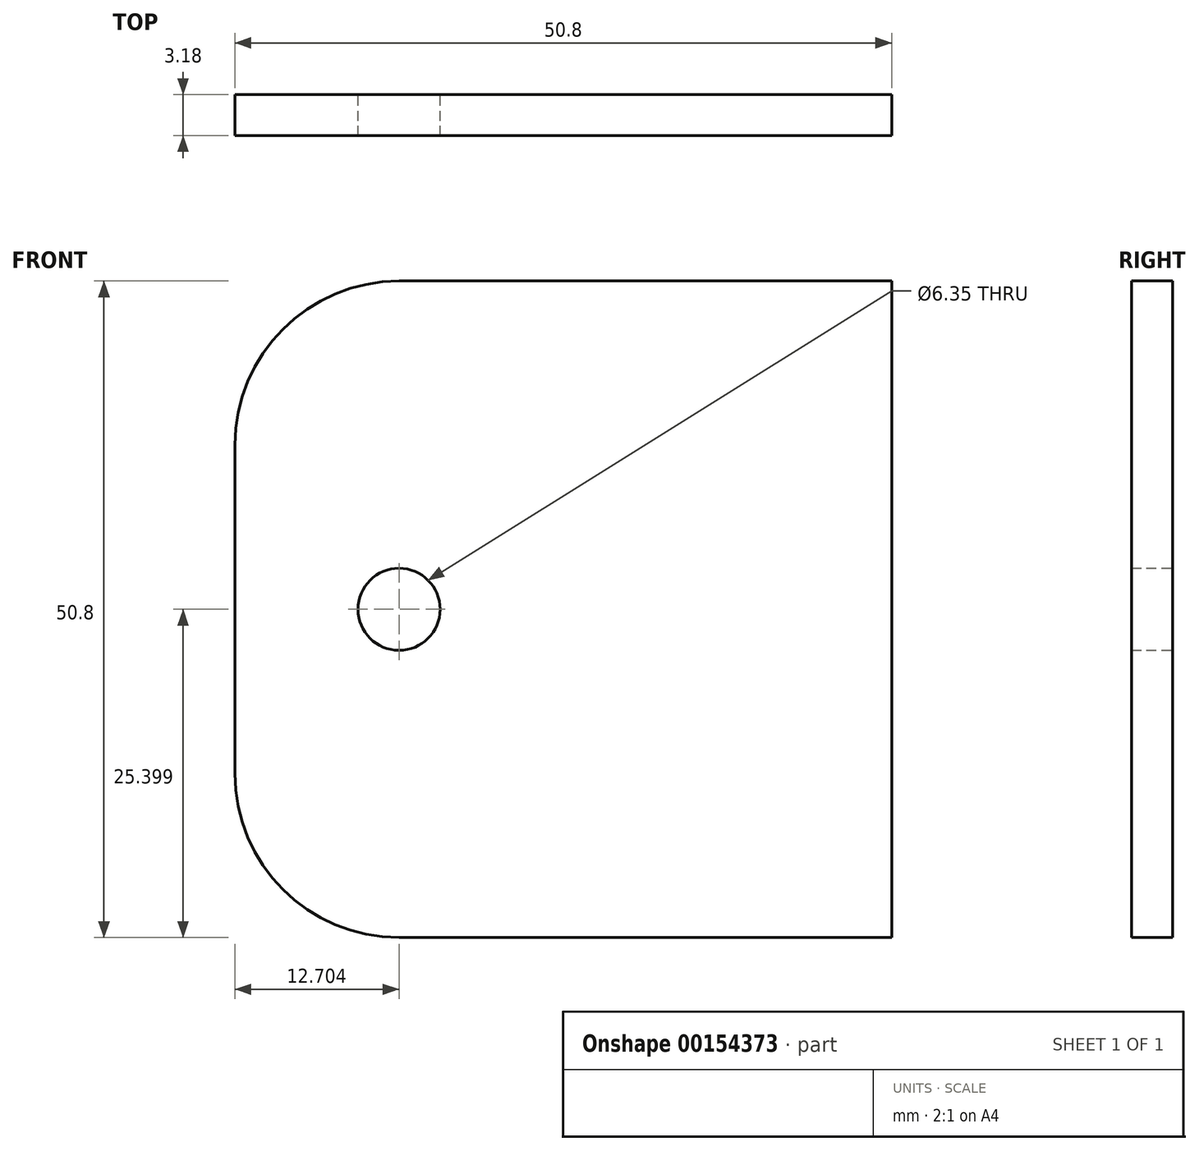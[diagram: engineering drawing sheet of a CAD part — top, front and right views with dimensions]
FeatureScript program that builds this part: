
annotation { "Feature Type Name" : "Feature", "Feature Type Description" : "" }
export const myFeature = defineFeature(function(context is Context, id is Id, definition is map)
    precondition{}
    {
        {
            var Q0;
            Q0=qCreatedBy(makeId("Front.planeOp"),FACE);
            var sketch = newSketch(context, id + "F0", { "sketchPlane" : qUnion([Q0])});
            skLineSegment(sketch, "E0.bottom", {"start": v(34.66, 38.44) * mm, "end": v(72.76, 38.44) * mm});
            skLineSegment(sketch, "E0.top", {"start": v(34.66, -12.36) * mm, "end": v(72.76, -12.36) * mm});
            skLineSegment(sketch, "E0.left", {"start": v(21.96, 25.74) * mm, "end": v(21.96, 0.34) * mm});
            skLineSegment(sketch, "E0.right", {"start": v(72.76, 38.44) * mm, "end": v(72.76, -12.36) * mm});
            skPoint(sketch, "E1.visualSharp", {"position": v(21.96, 38.44) * mm});
            skArc(sketch, "E1.filletArc", {"start": v(34.66, 38.44) * mm, "mid": v(25.68, 34.72) * mm, "end": v(21.96, 25.74) * mm});
            skPoint(sketch, "E2.visualSharp", {"position": v(21.96, -12.36) * mm});
            skArc(sketch, "E2.filletArc", {"start": v(21.96, 0.34) * mm, "mid": v(25.68, -8.64) * mm, "end": v(34.66, -12.36) * mm});
            skCircle(sketch, "E3", {"center": v(34.66, 13.04) * mm, "radius": 3.18 * mm});
            skPoint(sketch, "E4.orphan", {"position": v(72.76, 13.04) * mm});
            skPoint(sketch, "E5.start.orphan", {"position": v(21.96, 13.04) * mm});
            skSolve(sketch);
        }
        {
            var Q0;
            Q0 = qSketchRegion(id + "F0", true);
            extrude(context, id + "F1", {"entities" : qUnion([Q0]), "depth" : 3.17 * mm});
        }
    });
